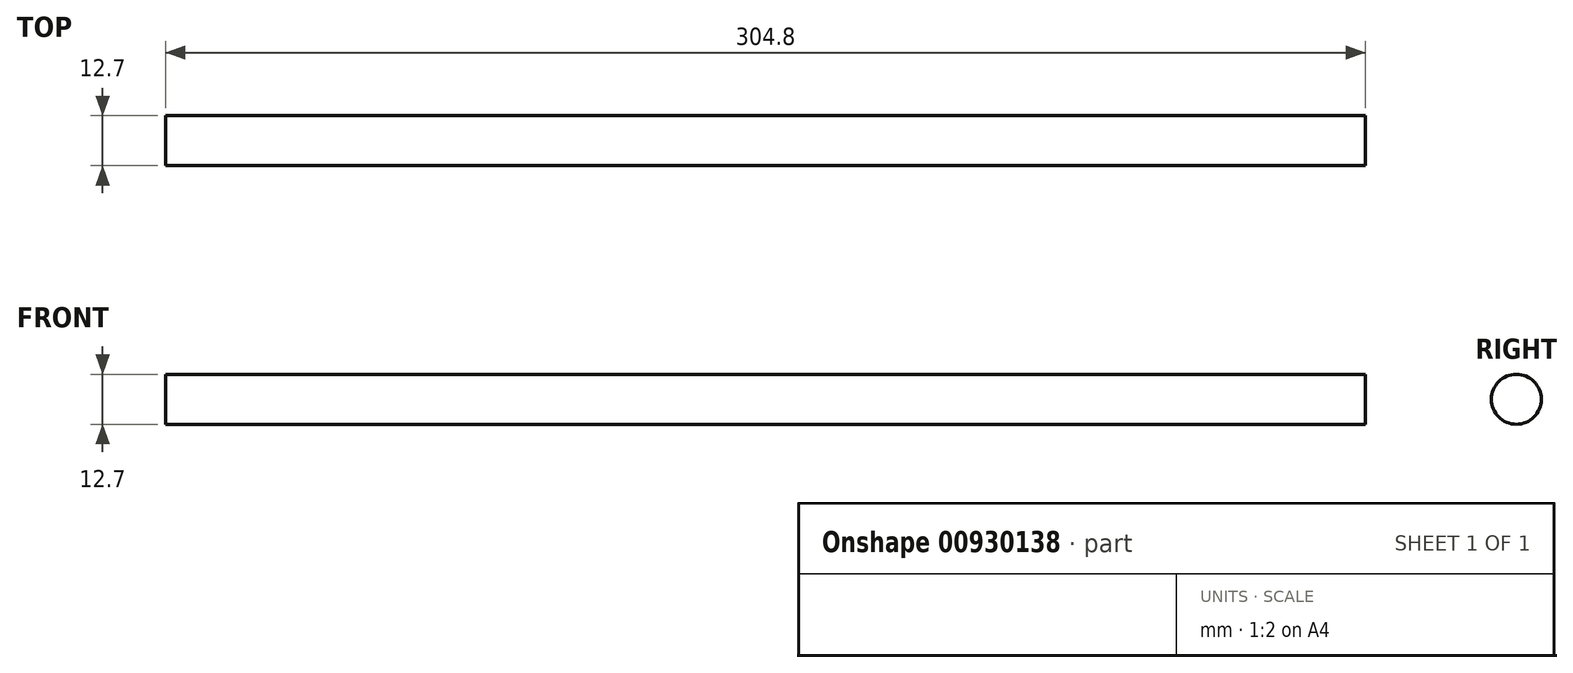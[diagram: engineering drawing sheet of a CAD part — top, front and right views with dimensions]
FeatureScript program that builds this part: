
annotation { "Feature Type Name" : "Feature", "Feature Type Description" : "" }
export const myFeature = defineFeature(function(context is Context, id is Id, definition is map)
    precondition{}
    {
        {
            var Q0;
            Q0=qCreatedBy(makeId("Right.planeOp"),FACE);
            var sketch = newSketch(context, id + "F0", { "sketchPlane" : qUnion([Q0])});
            skCircle(sketch, "E0", {"center": v(0, 0) * mm, "radius": 6.35 * mm});
            skSolve(sketch);
        }
        {
            var Q0;
            Q0 = qSketchRegion(id + "F0", true);
            extrude(context, id + "F1", {"entities" : qUnion([Q0]), "depth" : 304.8 * mm, "offsetDistance" : 25.4 * mm});
        }
    });
